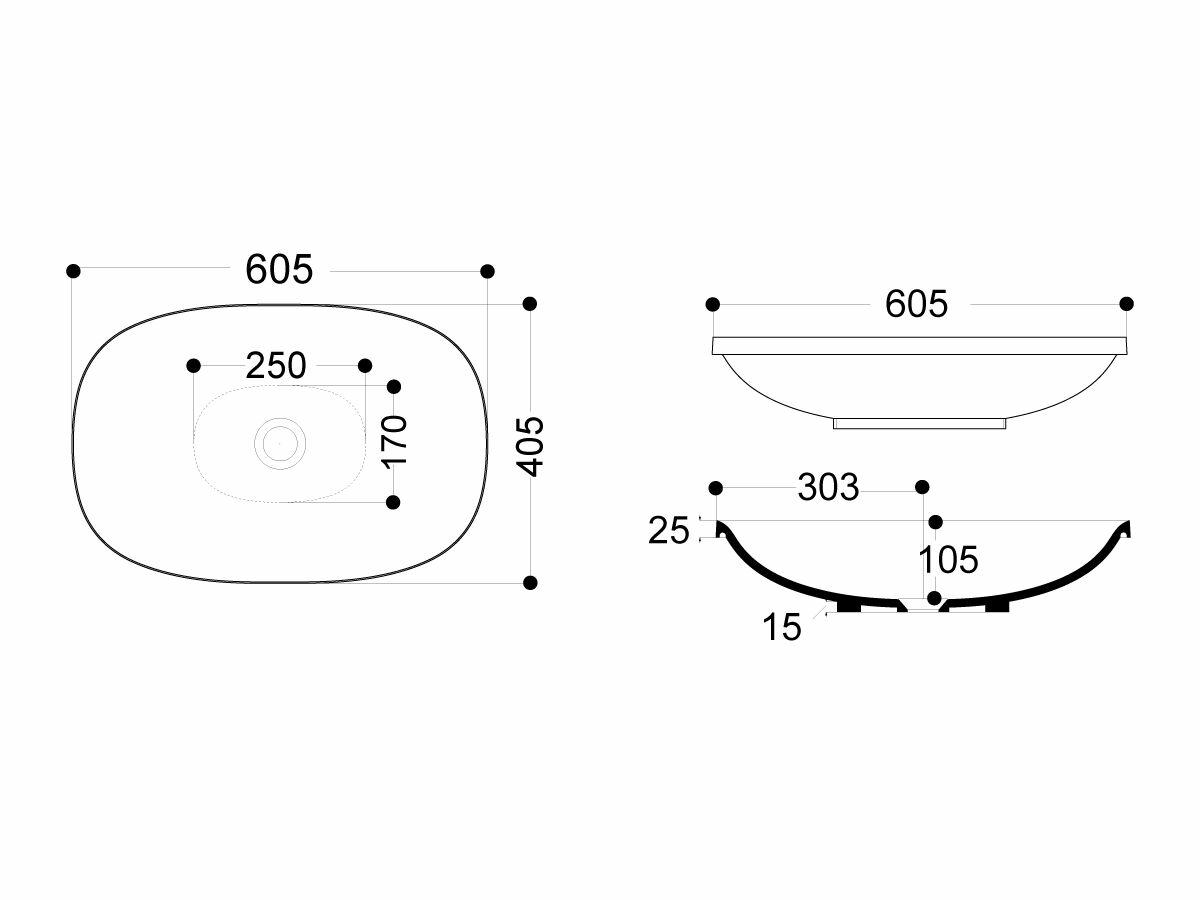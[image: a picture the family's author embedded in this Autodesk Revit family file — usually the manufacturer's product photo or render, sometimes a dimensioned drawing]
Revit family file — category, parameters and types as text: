
# Revit family: Reece_Basin_AXA_Wild_Semi Inset Basin_605 mm
name_source: partatom
category: Plumbing Fixtures
revit_build: Autodesk Revit 2018 (Build: 20190510_1515(x64)
units: mm (PartAtom-declared; Revit-internal decimal feet)

## family parameters
Cut with Voids When Loaded = No
Host = Face
Part Type = Normal
Room Calculation Point = Yes
Round Connector Dimension = Use Diameter
Shared = Yes

## types (1)
- 605 mm_13 L_No Taphole_Fine Fire Clay Ceramic_White
    CWFU = 0
    Default Elevation = 1000 mm  [stored 3.28084 ft]
    Description = AXA Wild Semi Inset Basin 600mm No Taphole
    Disclaimer = THIS FILE IS THE PROPERTY OF THE REECE GROUP. IT MAY NOT BE REPRODUCED, REVERSE-ENGINEERED OR MODIFIED. ANY REPUBLICATION, TRANSMISSION OR DISTRIBUTION FOR THE PURPOSE OF COMMERCIALLY EXPLOITING THE FILES IS PROHIBITED.
    HWFU = 0
    Keynote = Product #9508540, Reece_Basin_AXA_Wild_Semi Inset Basin_605 mm - 605 mm_13 L_No Taphole_Fine Fire Clay Ceramic_White
    Manufacturer = AXA
    Model = Wild
    Reece_Basin_Outlet = 32 mm  [stored 0.104987 ft]
    Reece_Detail_Additional = Semi Inset Basin
    Reece_Detail_Disclaimer = THIS FILE IS THE PROPERTY OF THE REECE GROUP. IT MAY NOT BE REPRODUCED, REVERSE-ENGINEERED OR MODIFIED. ANY REPUBLICATION, TRANSMISSION OR DISTRIBUTION FOR THE PURPOSE OF COMMERCIALLY EXPLOITING THE FILES IS PROHIBITED.
    Reece_Material-Main = Reece_Ceramic_Fine Fire Clay_White
    Reece_Material_Secondary = Reece_Brass_Chrome
    Reece_Overall_Capacity = 13 L
    Reece_Overall_Length = 405 mm
    Reece_Overall_Width = 605 mm  [stored 1.98491 ft]
    Reece_Product_Brand = AXA
    Reece_Product_Description = AXA Wild Semi Inset Basin 600mm No Taphole
    Reece_Product_Mount = Semi Inset
    Reece_Product_Number = 9508540
    Reece_Product_Sub Brand = Wild
    Reece_Product_Type = Basin
    Reece_Product_Web Page = https://www.reece.com.au
    Type Comments = Basin
    URL = https://www.reece.com.au
    WFU = 0

note: [stored X ft] marks values corroborated as IEEE doubles in the binary element streams (Revit-internal decimal feet)

## geometry (parser evidence)
native form markers: Sweep x2
no freeform markers — native parametric forms only
